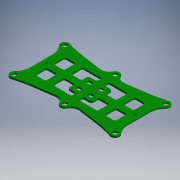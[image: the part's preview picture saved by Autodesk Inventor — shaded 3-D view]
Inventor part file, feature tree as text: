
AUTODESK INVENTOR PART (.ipt)
format: ipt  version: 2017 (Build 210142000, 142)  size: 382,464 bytes
history: native  units: mm (DEFAULTED — no unit token found)
features: fillet x5, extrude x4, sketch x4
ambient origin geometry x8: Origin, YZ Plane, XZ Plane, XY Plane, X Axis, Y Axis, Z Axis, Center Point
bodies: Solid1 (feature_tree)
feature tree (13):
  extrude  "Extrusion1"  Depth=24.0mm
  fillet  "Fillet3"  Radius=24.0mm
  fillet  "Fillet4"  Radius=24.0mm
  fillet  "Fillet5"  Radius=24.0mm
  fillet  "Fillet6"  Radius=24.0mm
  extrude  "Extrusion3"  Depth=24.0mm
  fillet  "Fillet7"  Radius=150.0mm
  extrude  "Extrusion4"  Depth=24.0mm
  extrude  "Extrusion5"  Depth=48.0mm
  sketch  "Sketch1"  dims[d6=5.0mm d7=0.0mm d27=24.0mm d28=24.0mm d30=24.0mm d32=24.0mm d34=24.0mm]
  sketch  "Sketch5"  dims[d36=24.0mm d40=150.0mm d42=150.0mm]
  sketch  "Sketch6"  dims[d43=12.0mm d44=24.0mm]
  sketch  "Sketch7"  dims[d45=360.0mm d46=48.0mm d47=25.0mm d48=30.0mm d49=70.0mm d50=61.5mm d51=10.0mm d52=10.0mm d53=20.0mm d54=20.0mm d55=20.0mm d56=20.0mm d57=10.0mm d58=0.0mm d59=5.0mm d60=13.0mm d61=10.0mm d62=0.0mm d63=2.75mm d64=29.0mm d65=24.5mm d69=10.0mm d70=0.0mm d71=5.0mm d72=10.0mm d73=10.0mm]
